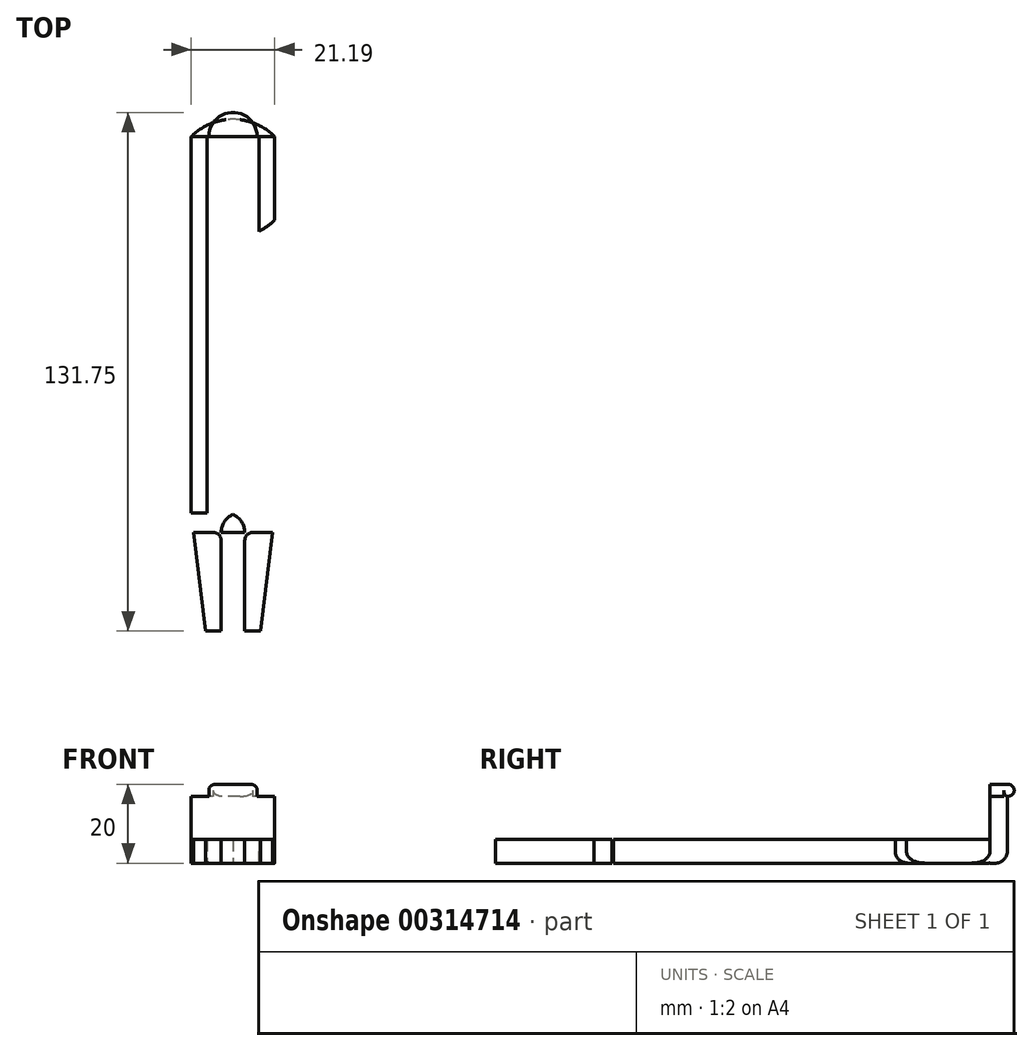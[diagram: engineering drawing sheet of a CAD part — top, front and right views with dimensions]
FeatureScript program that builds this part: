
annotation { "Feature Type Name" : "Feature", "Feature Type Description" : "" }
export const myFeature = defineFeature(function(context is Context, id is Id, definition is map)
    precondition{}
    {
        {
            var Q0;
            Q0=qCreatedBy(makeId("Top.planeOp"),FACE);
            var sketch = newSketch(context, id + "F0", { "sketchPlane" : qUnion([Q0])});
            skCircle(sketch, "E0", {"center": v(-47.92, 57.64) * mm, "radius": 15 * mm});
            skLineSegment(sketch, "E1", {"start": v(-58.5, 68.26) * mm, "end": v(-58.5, -13.2) * mm});
            skPoint(sketch, "E2", {"position": v(-47.92, -27.36) * mm});
            skLineSegment(sketch, "E3", {"start": v(-37.32, 68.26) * mm, "end": v(-37.32, -27.36) * mm});
            skLineSegment(sketch, "E4", {"start": v(-37.32, -27.36) * mm, "end": v(-58.5, -27.36) * mm});
            skLineSegment(sketch, "E5", {"start": v(-58.5, -27.36) * mm, "end": v(-58.5, -13.2) * mm});
            skPoint(sketch, "E6", {"position": v(-47.92, -57.36) * mm});
            skLineSegment(sketch, "E7", {"start": v(-47.92, -57.36) * mm, "end": v(-50.92, -57.36) * mm});
            skLineSegment(sketch, "E8", {"start": v(-50.92, -57.36) * mm, "end": v(-50.92, -27.36) * mm});
            skLineSegment(sketch, "E9", {"start": v(-47.92, -57.36) * mm, "end": v(-44.92, -57.36) * mm});
            skLineSegment(sketch, "E10", {"start": v(-44.92, -57.36) * mm, "end": v(-44.92, -27.36) * mm});
            skLineSegment(sketch, "E11", {"start": v(-50.92, -57.36) * mm, "end": v(-54.92, -57.36) * mm});
            skLineSegment(sketch, "E12", {"start": v(-54.92, -57.36) * mm, "end": v(-58.5, -27.36) * mm});
            skLineSegment(sketch, "E13", {"start": v(-44.92, -57.36) * mm, "end": v(-40.92, -57.36) * mm});
            skLineSegment(sketch, "E14", {"start": v(-40.92, -57.36) * mm, "end": v(-37.32, -27.36) * mm});
            skLineSegment(sketch, "E15", {"start": v(-58.5, 68.26) * mm, "end": v(-37.32, 68.26) * mm});
            skLineSegment(sketch, "E16", {"start": v(-58.5, -27.36) * mm, "end": v(-58.5, -17.08) * mm});
            skLineSegment(sketch, "E17", {"start": v(-58.5, -27.36) * mm, "end": v(-57.91, -32.33) * mm});
            skLineSegment(sketch, "E18", {"start": v(-57.91, -32.33) * mm, "end": v(-37.92, -32.33) * mm});
            skLineSegment(sketch, "E19", {"start": v(-37.92, -32.33) * mm, "end": v(-37.32, -27.36) * mm});
            skLineSegment(sketch, "E20", {"start": v(-58.5, -27.36) * mm, "end": v(-54.5, -27.36) * mm});
            skLineSegment(sketch, "E21", {"start": v(-54.5, -27.36) * mm, "end": v(-54.5, 68.26) * mm});
            skLineSegment(sketch, "E22", {"start": v(-37.32, -27.36) * mm, "end": v(-41.32, -27.36) * mm});
            skLineSegment(sketch, "E23", {"start": v(-41.32, 68.26) * mm, "end": v(-41.32, -27.36) * mm});
            skSolve(sketch);
        }
        {
            var Q0;
            {var subQ0=sQuery(id+"F0.wireOp",EDGE,"E15");var subQ4=makeQuery(id+"F0.imprint","INTERSECT",VERTEX,{"derivedFrom":[subQ0,sQuery(id+"F0.wireOp",EDGE,"E21")]});Q0=makeQuery(id+"F0.imprint","IMPRINT",FACE,{"disambiguationData":[TD([[makeQuery(id+"F0.imprint","IMPRINT",EDGE,{"disambiguationData":[TD([[subQ4,-1.0]])],"derivedFrom":subQ0}),1.0]])]});}
            var Q1;
            {var subQ0=sQuery(id+"F0.wireOp",EDGE,"E3");var subQ1=sQuery(id+"F0.wireOp",EDGE,"E0");var subQ2=makeQuery(id+"F0.imprint","INTERSECT",VERTEX,{"derivedFrom":[subQ1,subQ0]});Q1=makeQuery(id+"F0.imprint","IMPRINT",FACE,{"disambiguationData":[TD([[makeQuery(id+"F0.imprint","IMPRINT",EDGE,{"disambiguationData":[TD([[subQ2,1.0]])],"derivedFrom":subQ1}),1.0]])]});}
            var Q2;
            {var subQ0=sQuery(id+"F0.wireOp",EDGE,"E1");var subQ1=sQuery(id+"F0.wireOp",EDGE,"E0");var subQ2=makeQuery(id+"F0.imprint","INTERSECT",VERTEX,{"derivedFrom":[subQ1,subQ0]});Q2=makeQuery(id+"F0.imprint","IMPRINT",FACE,{"disambiguationData":[TD([[makeQuery(id+"F0.imprint","IMPRINT",EDGE,{"disambiguationData":[TD([[subQ2,-1.0]])],"derivedFrom":subQ1}),1.0]])]});}
            var Q3;
            {var subQ0=sQuery(id+"F0.wireOp",EDGE,"E5");Q3=makeQuery(id+"F0.imprint","IMPRINT",FACE,{"disambiguationData":[TD([[makeQuery(id+"F0.imprint","IMPRINT",EDGE,{"derivedFrom":subQ0}),-1.0]])]});}
            var Q4;
            {var subQ5=sQuery(id+"F0.wireOp",EDGE,"E22");Q4=makeQuery(id+"F0.imprint","IMPRINT",FACE,{"disambiguationData":[TD([[makeQuery(id+"F0.imprint","IMPRINT",EDGE,{"derivedFrom":subQ5}),-1.0]])]});}
            var Q5;
            {var subQ1=sQuery(id+"F0.wireOp",EDGE,"E17");Q5=makeQuery(id+"F0.imprint","IMPRINT",FACE,{"disambiguationData":[TD([[makeQuery(id+"F0.imprint","IMPRINT",EDGE,{"derivedFrom":subQ1}),1.0]])]});}
            var Q6;
            {var subQ0=sQuery(id+"F0.wireOp",EDGE,"E8");var subQ1=sQuery(id+"F0.wireOp",EDGE,"E4");var subQ2=makeQuery(id+"F0.imprint","INTERSECT",VERTEX,{"derivedFrom":[subQ1,subQ0]});Q6=makeQuery(id+"F0.imprint","IMPRINT",FACE,{"disambiguationData":[TD([[makeQuery(id+"F0.imprint","IMPRINT",EDGE,{"disambiguationData":[TD([[subQ2,1.0]])],"derivedFrom":subQ1}),1.0]])]});}
            var Q7;
            {var subQ0=sQuery(id+"F0.wireOp",EDGE,"E19");Q7=makeQuery(id+"F0.imprint","IMPRINT",FACE,{"disambiguationData":[TD([[makeQuery(id+"F0.imprint","IMPRINT",EDGE,{"derivedFrom":subQ0}),1.0]])]});}
            var Q8;
            {var subQ0=sQuery(id+"F0.wireOp",EDGE,"E13");Q8=makeQuery(id+"F0.imprint","IMPRINT",FACE,{"disambiguationData":[TD([[makeQuery(id+"F0.imprint","IMPRINT",EDGE,{"derivedFrom":subQ0}),1.0]])]});}
            var Q9;
            {var subQ0=sQuery(id+"F0.wireOp",EDGE,"E11");Q9=makeQuery(id+"F0.imprint","IMPRINT",FACE,{"disambiguationData":[TD([[makeQuery(id+"F0.imprint","IMPRINT",EDGE,{"derivedFrom":subQ0}),-1.0]])]});}
            extrude(context, id + "F1", {"entities" : qUnion([Q0, Q1, Q2, Q3, Q4, Q5, Q6, Q7, Q8, Q9]), "depth" : 6 * mm});
        }
        {
            var Q0;
            {var subQ0=sQuery(id+"F0.wireOp",EDGE,"E15");var subQ4=makeQuery(id+"F0.imprint","INTERSECT",VERTEX,{"derivedFrom":[subQ0,sQuery(id+"F0.wireOp",EDGE,"E21")]});Q0=makeQuery(id+"F0.imprint","IMPRINT",FACE,{"disambiguationData":[TD([[makeQuery(id+"F0.imprint","IMPRINT",EDGE,{"disambiguationData":[TD([[subQ4,-1.0]])],"derivedFrom":subQ0}),1.0]])]});}
            extrude(context, id + "F2", {"entities" : qUnion([Q0]), "operationType" : NewBodyOperationType.ADD, "depth" : 17 * mm});
        }
        {
            var Q0;
            Q0=makeQuery(id+"F2.opExtrude","CAP_FACE",FACE,{"disambiguationData":[OSD([sQuery(id+"F0.wireOp",EDGE,"E0"),sQuery(id+"F0.wireOp",EDGE,"E15")])],"isStart":false});
            var sketch = newSketch(context, id + "F3", { "sketchPlane" : qUnion([Q0])});
            skCircle(sketch, "E24", {"center": v(-47.92, 68.26) * mm, "radius": 6.13 * mm});
            skLineSegment(sketch, "E25", {"start": v(-54.05, 68.26) * mm, "end": v(-41.78, 68.26) * mm});
            skSolve(sketch);
        }
        {
            var Q0;
            {var subQ0=sQuery(id+"F3.wireOp",EDGE,"E24");var subQ1=makeQuery(id+"F2.opExtrude","CAP_EDGE",EDGE,{"disambiguationData":[OSD([sQuery(id+"F0.wireOp",EDGE,"E0")])],"isStart":false});var subQ2=makeQuery(id+"F3.imprint","INTERSECT",VERTEX,{"disambiguationData":[OD(0.0)],"derivedFrom":[subQ1,subQ0]});Q0=makeQuery(id+"F3.imprint","IMPRINT",FACE,{"disambiguationData":[TD([[makeQuery(id+"F3.imprint","IMPRINT",EDGE,{"disambiguationData":[TD([[subQ2,-1.0]])],"derivedFrom":subQ0}),1.0]])]});}
            var Q1;
            {var subQ0=sQuery(id+"F3.wireOp",EDGE,"E25");Q1=makeQuery(id+"F3.imprint","IMPRINT",FACE,{"disambiguationData":[TD([[makeQuery(id+"F3.imprint","IMPRINT",EDGE,{"derivedFrom":subQ0}),1.0]])]});}
            extrude(context, id + "F4", {"entities" : qUnion([Q0, Q1]), "operationType" : NewBodyOperationType.ADD, "depth" : 3 * mm});
        }
        {
            var Q0;
            {var subQ0=sQuery(id+"F3.wireOp",EDGE,"E24");Q0=makeQuery(id+"F4.boolean.opBoolean","SPLIT",EDGE,{"disambiguationData":[topologyDisambiguationEdgeConnected([makeQuery(id+"F4.opExtrude","SWEPT_FACE",FACE,{"disambiguationData":[OSD([subQ0])]}),makeQuery(id+"F4.opExtrude","CAP_FACE",FACE,{"disambiguationData":[OSD([subQ0,sQuery(id+"F3.wireOp",EDGE,"E25")])],"isStart":true})])],"derivedFrom":makeQuery(id+"F4.opExtrude","CAP_EDGE",EDGE,{"disambiguationData":[OSD([subQ0])],"isStart":true})});}
            var Q1;
            Q1=makeQuery(id+"F4.opExtrude","CAP_EDGE",EDGE,{"disambiguationData":[OSD([sQuery(id+"F3.wireOp",EDGE,"E24")])],"isStart":false});
            fillet(context, id + "F5", {"entities" : qUnion([Q0, Q1]), "radius" : 1.5 * mm, "tangentPropagation" : true, "allowEdgeOverflow" : false});
        }
        {
            var Q0;
            Q0=makeQuery(id+"F1.opExtrude","CAP_EDGE",EDGE,{"disambiguationData":[OSD([sQuery(id+"F0.wireOp",EDGE,"E0")])],"isStart":true});
            fillet(context, id + "F6", {"entities" : qUnion([Q0]), "radius" : 3 * mm, "tangentPropagation" : true, "allowEdgeOverflow" : false});
        }
        {
            var Q0;
            Q0=makeQuery(id+"F1.opExtrude","SWEPT_EDGE",EDGE,{"disambiguationData":[OSD([sQuery(id+"F0.wireOp",EDGE,"E15"),sQuery(id+"F0.wireOp",EDGE,"E21")])]});
            var Q1;
            Q1=makeQuery(id+"F1.opExtrude","SWEPT_EDGE",EDGE,{"disambiguationData":[OSD([sQuery(id+"F0.wireOp",EDGE,"E15"),sQuery(id+"F0.wireOp",EDGE,"E23")])]});
            var Q2;
            Q2=makeQuery(id+"F1.opExtrude","SWEPT_EDGE",EDGE,{"disambiguationData":[OSD([sQuery(id+"F0.wireOp",EDGE,"E4"),sQuery(id+"F0.wireOp",EDGE,"E22"),sQuery(id+"F0.wireOp",EDGE,"E23")])]});
            var Q3;
            Q3=makeQuery(id+"F1.opExtrude","SWEPT_EDGE",EDGE,{"disambiguationData":[OSD([sQuery(id+"F0.wireOp",EDGE,"E4"),sQuery(id+"F0.wireOp",EDGE,"E20"),sQuery(id+"F0.wireOp",EDGE,"E21")])]});
            fillet(context, id + "F7", {"entities" : qUnion([Q0, Q1, Q2, Q3]), "radius" : 5 * mm, "tangentPropagation" : true, "allowEdgeOverflow" : false});
        }
        {
            var Q0;
            Q0=makeQuery(id+"F1.opExtrude","SWEPT_EDGE",EDGE,{"disambiguationData":[OSD([sQuery(id+"F0.wireOp",EDGE,"E10"),sQuery(id+"F0.wireOp",EDGE,"E18")])]});
            var Q1;
            Q1=makeQuery(id+"F1.opExtrude","SWEPT_EDGE",EDGE,{"disambiguationData":[OSD([sQuery(id+"F0.wireOp",EDGE,"E8"),sQuery(id+"F0.wireOp",EDGE,"E18")])]});
            fillet(context, id + "F8", {"entities" : qUnion([Q0, Q1]), "radius" : 2 * mm, "tangentPropagation" : true, "allowEdgeOverflow" : false});
        }
    });
